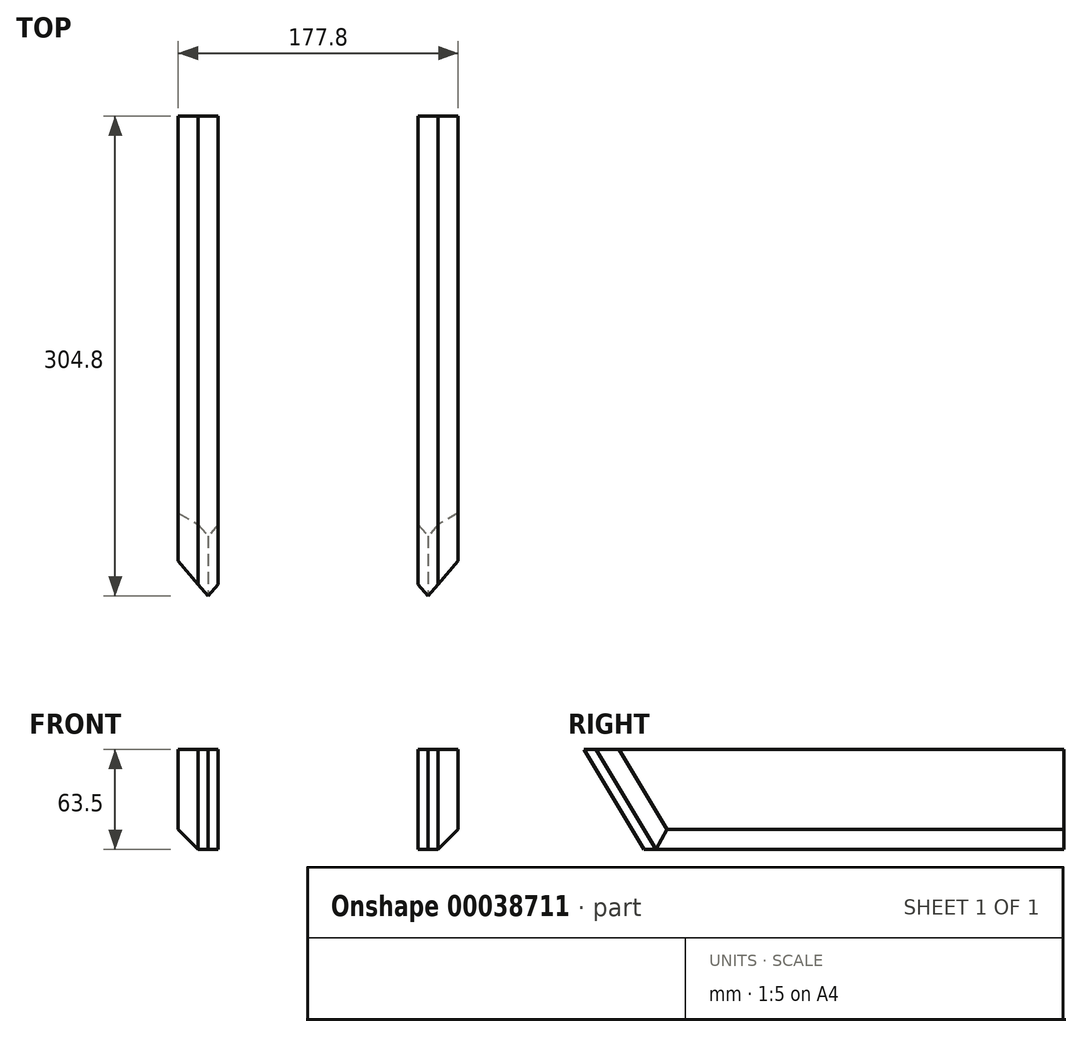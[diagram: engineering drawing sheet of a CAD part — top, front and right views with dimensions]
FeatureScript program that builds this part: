
annotation { "Feature Type Name" : "Feature", "Feature Type Description" : "" }
export const myFeature = defineFeature(function(context is Context, id is Id, definition is map)
    precondition{}
    {
        {
            var Q0;
            Q0=qCreatedBy(makeId("Right.planeOp"),FACE);
            var sketch = newSketch(context, id + "F0", { "sketchPlane" : qUnion([Q0])});
            skLineSegment(sketch, "E0", {"start": v(-152.4, 31.75) * mm, "end": v(152.4, 31.75) * mm});
            skLineSegment(sketch, "E1", {"start": v(152.4, -31.75) * mm, "end": v(152.4, 31.75) * mm});
            skLineSegment(sketch, "E2", {"start": v(152.4, -31.75) * mm, "end": v(-114.3, -31.75) * mm});
            skLineSegment(sketch, "E3", {"start": v(-152.4, 31.75) * mm, "end": v(-114.3, -31.75) * mm});
            skSolve(sketch);
        }
        {
            var Q0;
            Q0 = qSketchRegion(id + "F0", true);
            extrude(context, id + "F1", {"entities" : qUnion([Q0]), "depth" : 12.7 * mm});
        }
        {
            var Q0;
            Q0=makeQuery(id+"F1.opExtrude","CAP_EDGE",EDGE,{"disambiguationData":[OSD([sQuery(id+"F0.wireOp",EDGE,"E3")])],"isStart":false});
            chamfer(context, id + "F2", {"entities" : qUnion([Q0]), "chamferType" : ChamferType.OFFSET_ANGLE, "width" : 6.35 * mm, "oppositeDirection" : false, "angle" : 45 * degree, "tangentPropagation" : true});
        }
        {
            var Q0;
            Q0=makeQuery(id+"F1.opExtrude","CAP_EDGE",EDGE,{"disambiguationData":[OSD([sQuery(id+"F0.wireOp",EDGE,"E3")])],"isStart":true});
            chamfer(context, id + "F3", {"entities" : qUnion([Q0]), "chamferType" : ChamferType.OFFSET_ANGLE, "width" : 6.35 * mm, "oppositeDirection" : false, "angle" : 45 * degree, "tangentPropagation" : true});
        }
        {
            var Q0;
            Q0=makeQuery(id+"F1.opExtrude","CAP_FACE",FACE,{"disambiguationData":[OSD([sQuery(id+"F0.wireOp",EDGE,"E0"),sQuery(id+"F0.wireOp",EDGE,"E1"),sQuery(id+"F0.wireOp",EDGE,"E2"),sQuery(id+"F0.wireOp",EDGE,"E3")])],"isStart":false});
            var sketch = newSketch(context, id + "F4", { "sketchPlane" : qUnion([Q0])});
            skLineSegment(sketch, "E4", {"start": v(-145, 31.75) * mm, "end": v(152.4, 31.75) * mm});
            skLineSegment(sketch, "E5", {"start": v(152.4, 31.75) * mm, "end": v(152.4, -31.75) * mm});
            skLineSegment(sketch, "E6", {"start": v(152.4, -31.75) * mm, "end": v(-106.9, -31.75) * mm});
            skLineSegment(sketch, "E7", {"start": v(-106.9, -31.75) * mm, "end": v(-145, 31.75) * mm});
            skSolve(sketch);
        }
        {
            var Q0;
            Q0=makeQuery(id+"F4.imprint","IMPRINT",FACE,{"disambiguationData":[TD([[makeQuery(id+"F4.imprint","IMPRINT",EDGE,{"derivedFrom":sQuery(id+"F4.wireOp",EDGE,"E4")}),-1.0]])]});
            extrude(context, id + "F5", {"entities" : qUnion([Q0]), "depth" : 12.7 * mm});
        }
        {
            var Q0;
            Q0=makeQuery(id+"F5.opExtrude","CAP_EDGE",EDGE,{"disambiguationData":[OSD([sQuery(id+"F4.wireOp",EDGE,"E7")])],"isStart":false});
            chamfer(context, id + "F6", {"entities" : qUnion([Q0]), "chamferType" : ChamferType.OFFSET_ANGLE, "width" : 12.7 * mm, "oppositeDirection" : false, "angle" : 45 * degree, "tangentPropagation" : true});
        }
        {
            var Q0;
            Q0=makeQuery(id+"F5.opExtrude","CAP_EDGE",EDGE,{"disambiguationData":[OSD([sQuery(id+"F4.wireOp",EDGE,"E6")])],"isStart":false});
            chamfer(context, id + "F7", {"entities" : qUnion([Q0]), "chamferType" : ChamferType.OFFSET_ANGLE, "width" : 12.7 * mm, "oppositeDirection" : false, "angle" : 45 * degree, "tangentPropagation" : true});
        }
        {
            var Q0;
            Q0=makeQuery(id+"F1.opExtrude","SWEPT_BODY",BODY,{"disambiguationData":[OSD([sQuery(id+"F0.wireOp",EDGE,"E0"),sQuery(id+"F0.wireOp",EDGE,"E1"),sQuery(id+"F0.wireOp",EDGE,"E2"),sQuery(id+"F0.wireOp",EDGE,"E3")])]});
            var Q1;
            Q1=makeQuery(id+"F5.opExtrude","SWEPT_BODY",BODY,{"disambiguationData":[OSD([sQuery(id+"F4.wireOp",EDGE,"E4"),sQuery(id+"F4.wireOp",EDGE,"E5"),sQuery(id+"F4.wireOp",EDGE,"E6"),sQuery(id+"F4.wireOp",EDGE,"E7")])]});
            transform(context, id + "F8", {"entities" : qUnion([Q0, Q1]), "transformType" : TransformType.TRANSLATION_3D, "dx" : 63.5 * mm, "dy" : 0 * mm, "dz" : 0 * mm, "makeCopy" : false});
        }
        {
            var Q0;
            Q0=makeQuery(id+"F1.opExtrude","SWEPT_BODY",BODY,{"disambiguationData":[OSD([sQuery(id+"F0.wireOp",EDGE,"E0"),sQuery(id+"F0.wireOp",EDGE,"E1"),sQuery(id+"F0.wireOp",EDGE,"E2"),sQuery(id+"F0.wireOp",EDGE,"E3")])]});
            var Q1;
            Q1=makeQuery(id+"F5.opExtrude","SWEPT_BODY",BODY,{"disambiguationData":[OSD([sQuery(id+"F4.wireOp",EDGE,"E4"),sQuery(id+"F4.wireOp",EDGE,"E5"),sQuery(id+"F4.wireOp",EDGE,"E6"),sQuery(id+"F4.wireOp",EDGE,"E7")])]});
            var Q2;
            Q2=qCreatedBy(makeId("Right.planeOp"),FACE);
            mirror(context, id + "F9", {"entities" : qUnion([Q0, Q1]), "mirrorPlane" : qUnion([Q2])});
        }
    });
